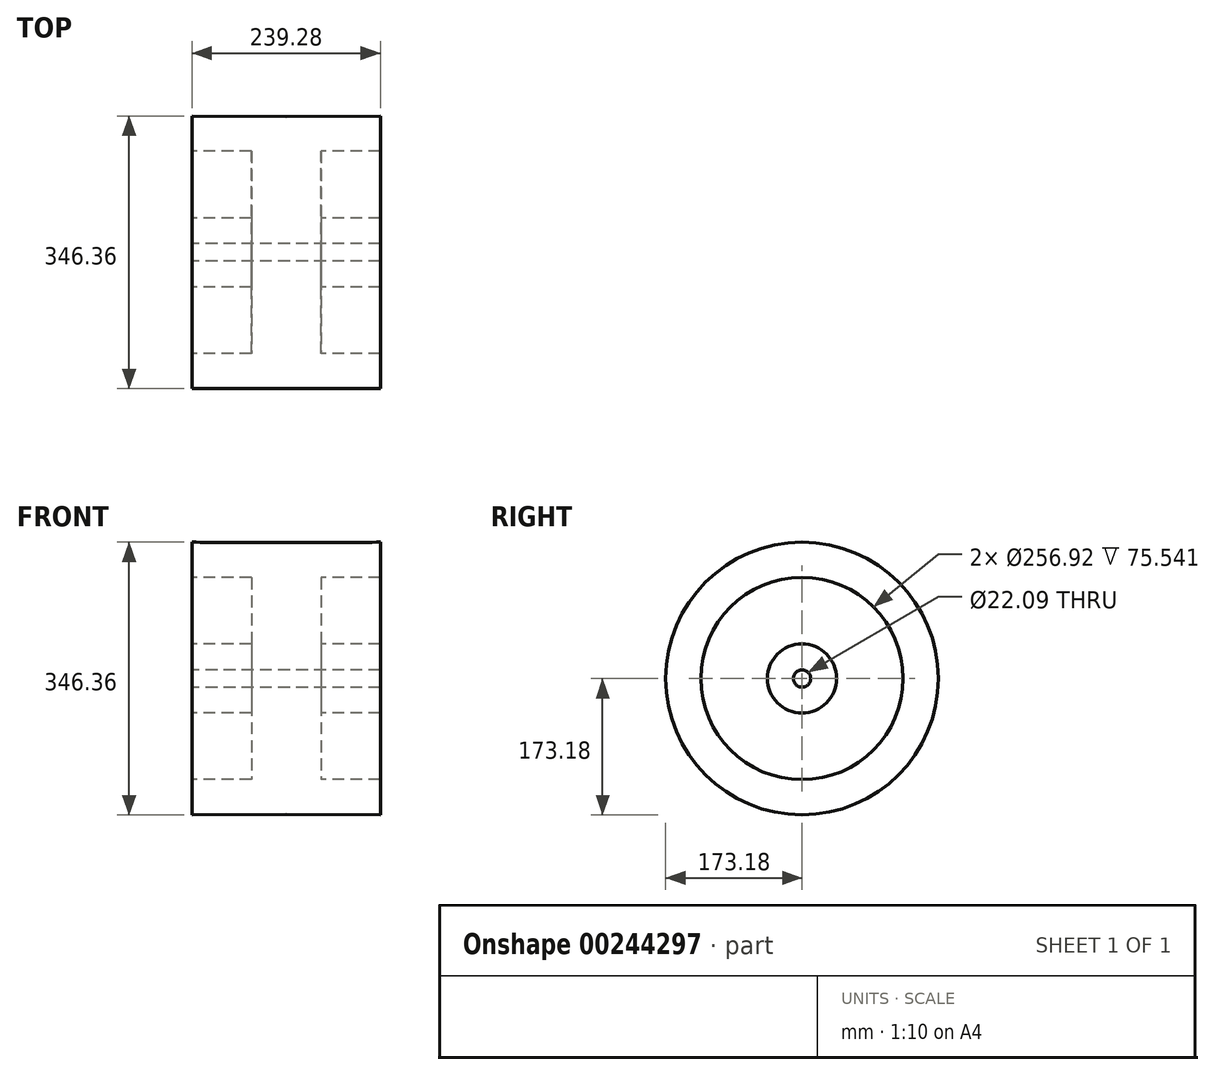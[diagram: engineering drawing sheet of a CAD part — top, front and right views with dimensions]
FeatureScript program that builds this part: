
annotation { "Feature Type Name" : "Feature", "Feature Type Description" : "" }
export const myFeature = defineFeature(function(context is Context, id is Id, definition is map)
    precondition{}
    {
        {
            var Q0;
            Q0=qCreatedBy(makeId("Front.planeOp"),FACE);
            var sketch = newSketch(context, id + "F0", { "sketchPlane" : qUnion([Q0])});
            skLineSegment(sketch, "E0", {"start": v(0, 0) * mm, "end": v(0, 189.22) * mm, "construction": true});
            skLineSegment(sketch, "E1", {"start": v(-0.24, 0) * mm, "end": v(137.7, 0) * mm, "construction": true});
            skLineSegment(sketch, "E2", {"start": v(119.64, 173.18) * mm, "end": v(119.64, 128.46) * mm});
            skLineSegment(sketch, "E3", {"start": v(119.64, 128.46) * mm, "end": v(44.1, 128.46) * mm});
            skLineSegment(sketch, "E4", {"start": v(44.1, 128.46) * mm, "end": v(44.1, 43.89) * mm});
            skLineSegment(sketch, "E5", {"start": v(44.1, 43.89) * mm, "end": v(119.64, 43.89) * mm});
            skLineSegment(sketch, "E6", {"start": v(119.64, 43.89) * mm, "end": v(119.64, 11.04) * mm});
            skLineSegment(sketch, "E7", {"start": v(119.64, 11.04) * mm, "end": v(0, 11.04) * mm});
            skLineSegment(sketch, "E8", {"start": v(-0.24, 172.8) * mm, "end": v(119.64, 173.18) * mm});
            skLineSegment(sketch, "E9.MirrorCS", {"start": v(0.24, 172.8) * mm, "end": v(-119.64, 173.18) * mm});
            skLineSegment(sketch, "E10.MirrorCS", {"start": v(-119.64, 173.18) * mm, "end": v(-119.64, 128.46) * mm});
            skLineSegment(sketch, "E11.MirrorCS", {"start": v(-119.64, 128.46) * mm, "end": v(-44.1, 128.46) * mm});
            skLineSegment(sketch, "E12.MirrorCS", {"start": v(-44.1, 128.46) * mm, "end": v(-44.1, 43.89) * mm});
            skLineSegment(sketch, "E13.MirrorCS", {"start": v(-44.1, 43.89) * mm, "end": v(-119.64, 43.89) * mm});
            skLineSegment(sketch, "E14.MirrorCS", {"start": v(-119.64, 43.89) * mm, "end": v(-119.64, 11.04) * mm});
            skLineSegment(sketch, "E15.MirrorCS", {"start": v(-119.64, 11.04) * mm, "end": v(0, 11.04) * mm});
            skSolve(sketch);
        }
        {
            var Q0;
            Q0 = qSketchRegion(id + "F0", true);
            var Q1;
            Q1=sQuery(id+"F0.wireOp",EDGE,"E1");
            revolve(context, id + "F1", {"entities" : qUnion([Q0]), "axis" : qUnion([Q1]), "revolveType" : RevolveType.FULL});
        }
    });
